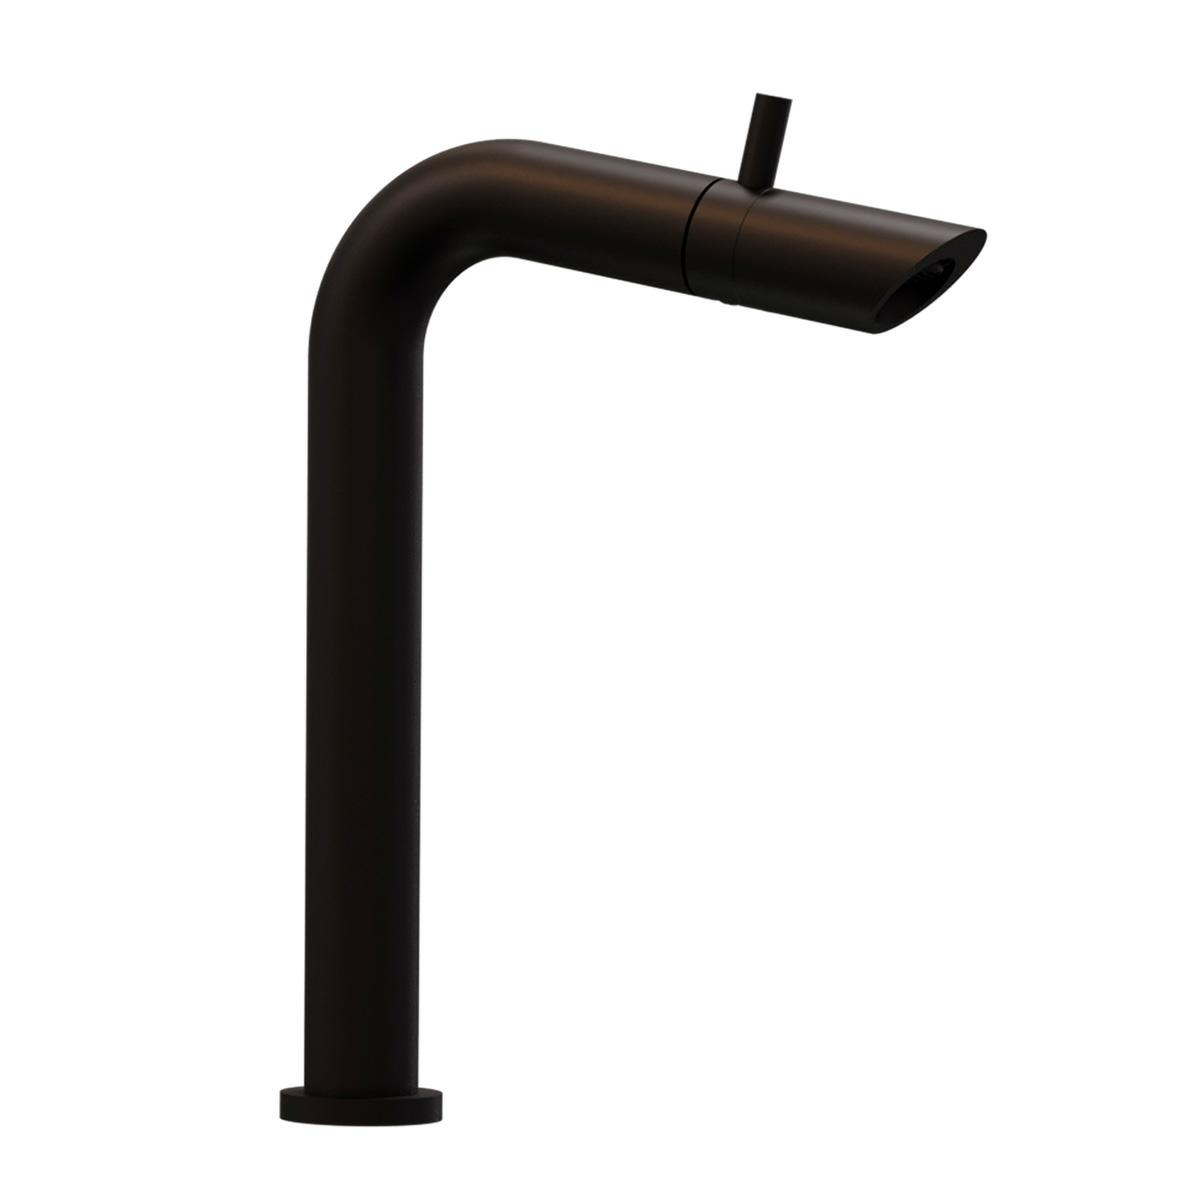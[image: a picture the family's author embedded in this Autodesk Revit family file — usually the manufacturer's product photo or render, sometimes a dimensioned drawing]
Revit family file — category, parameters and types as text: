
# Revit family: E-923-EB_RFA
name_source: partatom
category: Aparatos sanitarios
units: mm (PartAtom-declared; Revit-internal decimal feet)

## family parameters
Activar corte en vistas = No
Compartido = Sí
Corte con vacíos al cargar = No
Cota de conector redondo = Usar diámetro
Mantener orientación de anotación = No
Número OmniClass = 23.45.55.17
Punto de cálculo de habitación = Sí
Se basa en plano de trabajo = No
Siempre vertical = Sí
Tipo de pieza = Normal
Título OmniClass = Mixing Faucets

## types (1)
- E-923-EB
    Brass Chromed = Brass
    Comentarios de tipo = Monomando alto de lavabo. Control de flujo y temperatura con un solo movimiento. Incluye contra de push. Incluye inserto para usarse con lavabos sin rebosadero. Acabado Ébano. Presión mínima requerida 0.80 kg/cm2. Recomendado para lavabos de sobreponer.
    Descripción = Llave alta de lavabo Bamboo Ébano
    Elevación por defecto = 0"
    Fabricante = HELVEX S.A. de C.V.
    Imagen de tipo = E-923-EB.jpg
    Inlet Threads = ½" - 14 NPSM
    Max. Working Pressure = 85.3 psi
    Min. Working Pressure = 11.4 psi
    Modelo = E-923-EB
    Support Base Diameter = 2"
    Total Height = 12"
    Total Length = 8"
    Total Width = 1"
    URL = https://helvex.com.mx
    Ébano = Ébano

## geometry (parser evidence)
native form markers: Sweep x3
no freeform markers — native parametric forms only
